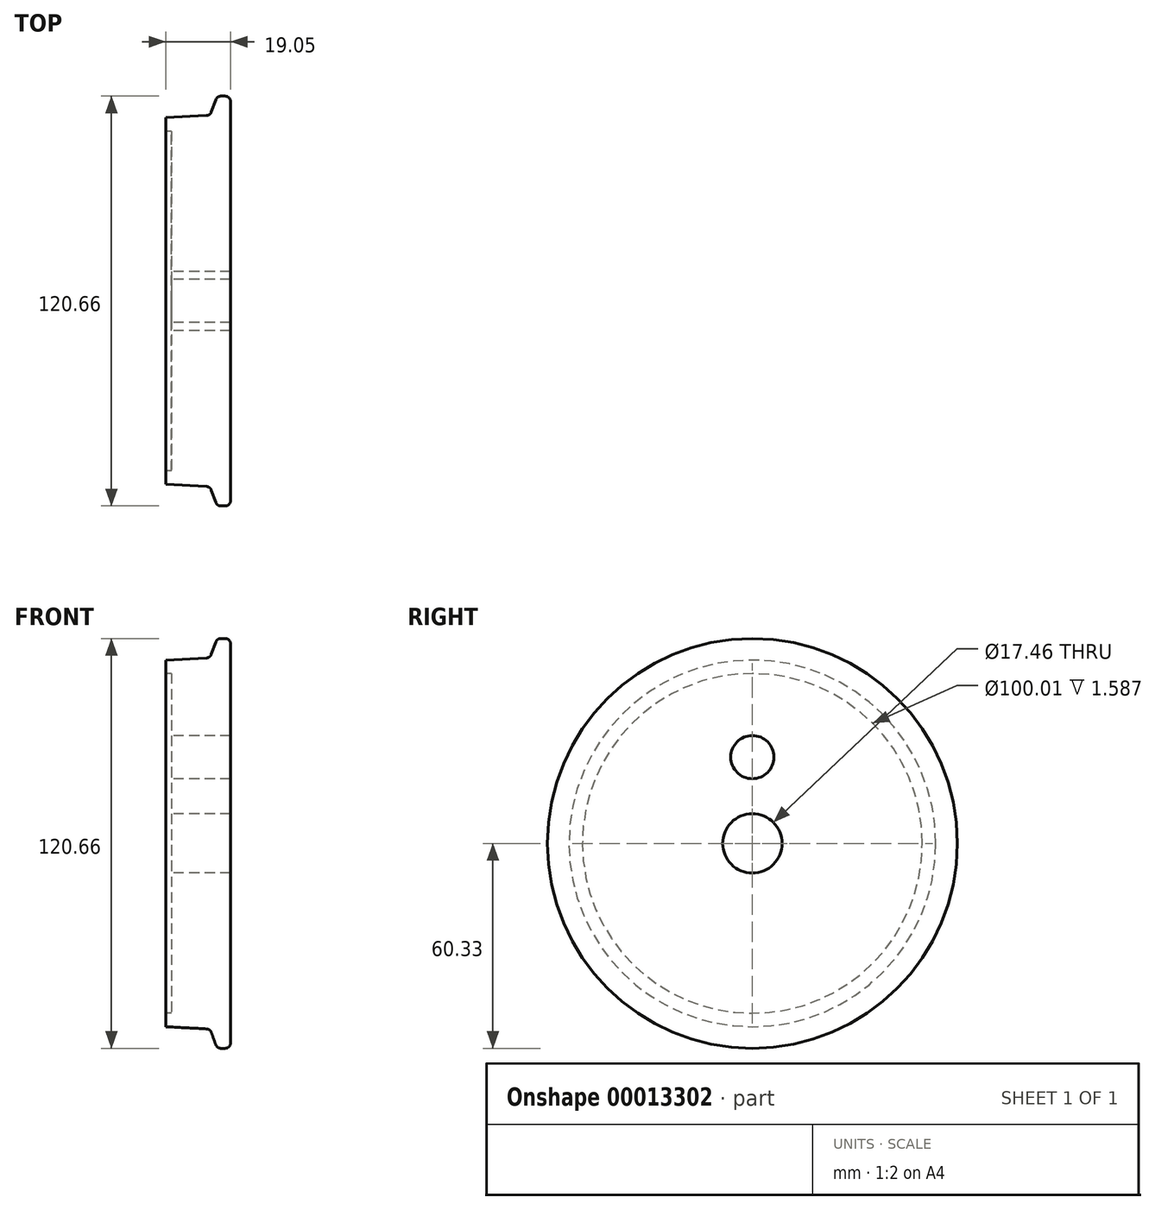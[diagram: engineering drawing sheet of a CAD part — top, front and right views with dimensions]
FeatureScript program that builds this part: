
annotation { "Feature Type Name" : "Feature", "Feature Type Description" : "" }
export const myFeature = defineFeature(function(context is Context, id is Id, definition is map)
    precondition{}
    {
        {
            var Q0;
            Q0=qCreatedBy(makeId("Top.planeOp"),FACE);
            var sketch = newSketch(context, id + "F0", { "sketchPlane" : qUnion([Q0])});
            skLineSegment(sketch, "E0.left", {"start": v(0, 0) * mm, "end": v(0, 53.98) * mm});
            skLineSegment(sketch, "E1", {"start": v(0, 53.98) * mm, "end": v(11.97, 54.6) * mm});
            skLineSegment(sketch, "E2", {"start": v(13.38, 55.64) * mm, "end": v(14.7, 59.28) * mm});
            skLineSegment(sketch, "E3", {"start": v(16.2, 60.33) * mm, "end": v(17.46, 60.33) * mm});
            skLineSegment(sketch, "E4", {"start": v(19.05, 58.74) * mm, "end": v(19.05, 0) * mm});
            skLineSegment(sketch, "E5", {"start": v(19.05, 0) * mm, "end": v(0, 0) * mm});
            skPoint(sketch, "E6.visualSharp", {"position": v(13.02, 54.66) * mm});
            skArc(sketch, "E6.filletArc", {"start": v(11.97, 54.6) * mm, "mid": v(12.83, 54.91) * mm, "end": v(13.38, 55.64) * mm});
            skPoint(sketch, "E7.visualSharp", {"position": v(15.08, 60.33) * mm});
            skArc(sketch, "E7.filletArc", {"start": v(16.2, 60.33) * mm, "mid": v(15.28, 60.04) * mm, "end": v(14.7, 59.28) * mm});
            skPoint(sketch, "E8.visualSharp", {"position": v(19.05, 60.33) * mm});
            skArc(sketch, "E8.filletArc", {"start": v(19.05, 58.74) * mm, "mid": v(18.59, 59.86) * mm, "end": v(17.46, 60.33) * mm});
            skSolve(sketch);
        }
        {
            var Q0;
            Q0=makeQuery(id+"F0.imprint","IMPRINT",FACE,{"disambiguationData":[TD([[makeQuery(id+"F0.imprint","IMPRINT",EDGE,{"derivedFrom":sQuery(id+"F0.wireOp",EDGE,"E0.left")}),-1.0]])]});
            var Q1;
            Q1=sQuery(id+"F0.wireOp",EDGE,"E5");
            revolve(context, id + "F1", {"entities" : qUnion([Q0]), "axis" : qUnion([Q1]), "revolveType" : RevolveType.FULL});
        }
        {
            var Q0;
            Q0=makeQuery(id+"F1.opRevolve","SWEPT_FACE",FACE,{"disambiguationData":[OSD([sQuery(id+"F0.wireOp",EDGE,"E0.left")])]});
            var sketch = newSketch(context, id + "F2", { "sketchPlane" : qUnion([Q0])});
            skCircle(sketch, "E9", {"center": v(0, 0) * mm, "radius": 8.73 * mm});
            skCircle(sketch, "E10", {"center": v(0, 25.4) * mm, "radius": 6.35 * mm});
            skSolve(sketch);
        }
        {
            var Q0;
            Q0 = qSketchRegion(id + "F2", true);
            extrude(context, id + "F3", {"entities" : qUnion([Q0]), "operationType" : NewBodyOperationType.REMOVE, "oppositeDirection" : true, "depth" : 25.4 * mm});
        }
        {
            var Q0;
            Q0=makeQuery(id+"F1.opRevolve","SWEPT_FACE",FACE,{"disambiguationData":[OSD([sQuery(id+"F0.wireOp",EDGE,"E0.left")])]});
            var sketch = newSketch(context, id + "F4", { "sketchPlane" : qUnion([Q0])});
            skCircle(sketch, "E11", {"center": v(0, 0) * mm, "radius": 50 * mm});
            skSolve(sketch);
        }
        {
            var Q0;
            Q0=makeQuery(id+"F4.imprint","IMPRINT",FACE,{"disambiguationData":[TD([[makeQuery(id+"F4.imprint","IMPRINT",EDGE,{"derivedFrom":sQuery(id+"F4.wireOp",EDGE,"E11")}),1.0]])]});
            extrude(context, id + "F5", {"entities" : qUnion([Q0]), "operationType" : NewBodyOperationType.REMOVE, "oppositeDirection" : true, "depth" : 1.59 * mm});
        }
    });
